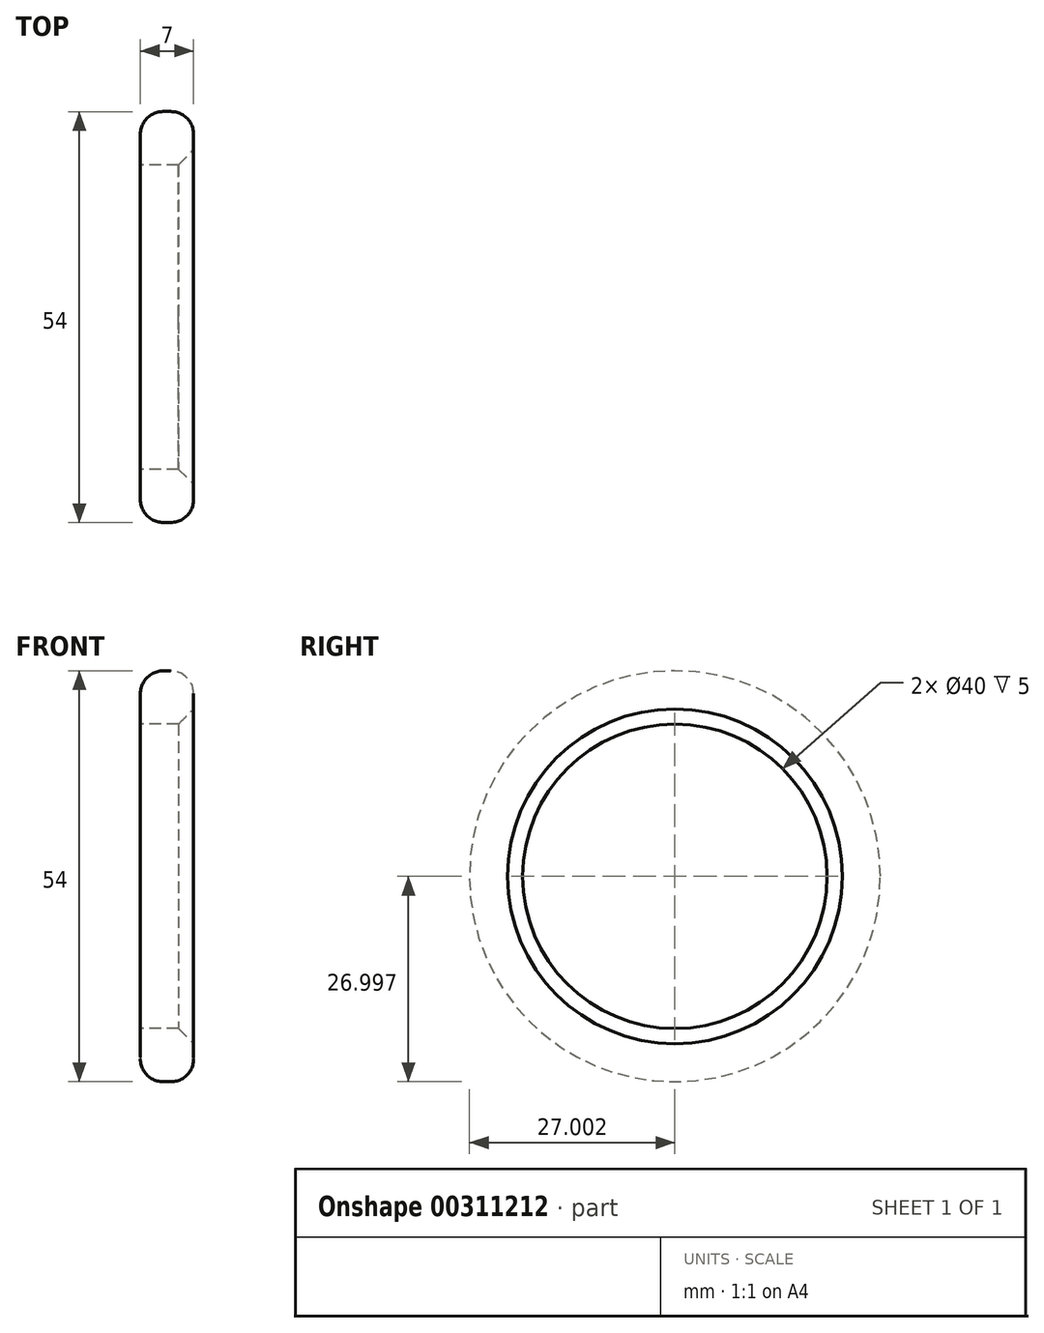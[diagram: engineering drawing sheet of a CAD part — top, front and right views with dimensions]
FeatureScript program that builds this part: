
annotation { "Feature Type Name" : "Feature", "Feature Type Description" : "" }
export const myFeature = defineFeature(function(context is Context, id is Id, definition is map)
    precondition{}
    {
        {
            var Q0;
            Q0=qCreatedBy(makeId("Top.planeOp"),FACE);
            var sketch = newSketch(context, id + "F0", { "sketchPlane" : qUnion([Q0])});
            skLineSegment(sketch, "E0", {"start": v(0, 0) * mm, "end": v(0, 4) * mm});
            skLineSegment(sketch, "E1", {"start": v(3, 7) * mm, "end": v(4, 7) * mm});
            skLineSegment(sketch, "E2", {"start": v(7, 4) * mm, "end": v(7, 2) * mm});
            skLineSegment(sketch, "E3", {"start": v(7, 2) * mm, "end": v(5, 0) * mm});
            skLineSegment(sketch, "E4", {"start": v(5, 0) * mm, "end": v(0, 0) * mm});
            skPoint(sketch, "E5.visualSharp", {"position": v(7, 7) * mm});
            skArc(sketch, "E5.filletArc", {"start": v(7, 4) * mm, "mid": v(6.12, 6.12) * mm, "end": v(4, 7) * mm});
            skPoint(sketch, "E6.visualSharp", {"position": v(0, 7) * mm});
            skArc(sketch, "E6.filletArc", {"start": v(3, 7) * mm, "mid": v(0.88, 6.12) * mm, "end": v(0, 4) * mm});
            skSolve(sketch);
        }
        {
            var Q0;
            Q0=qCreatedBy(makeId("Right.planeOp"),FACE);
            var sketch = newSketch(context, id + "F1", { "sketchPlane" : qUnion([Q0])});
            skCircle(sketch, "E7", {"center": v(-20, -0.3) * mm, "radius": 20 * mm});
            skPoint(sketch, "E7.first.point", {"position": v(0, 0) * mm});
            skPoint(sketch, "E7.second.point", {"position": v(-40, 0) * mm});
            skPoint(sketch, "E7.third.point", {"position": v(-20.22, 19.7) * mm});
            skSolve(sketch);
        }
        {
            var Q0;
            Q0=makeQuery(id+"F0.imprint","IMPRINT",FACE,{"disambiguationData":[TD([[makeQuery(id+"F0.imprint","IMPRINT",EDGE,{"derivedFrom":sQuery(id+"F0.wireOp",EDGE,"E0")}),-1.0]])]});
            var Q1;
            Q1=sQuery(id+"F1.wireOp",EDGE,"E7");
            revolve(context, id + "F2", {"entities" : qUnion([Q0]), "axis" : qUnion([Q1]), "revolveType" : RevolveType.FULL});
        }
        {
            var Q0;
            Q0=makeQuery(id+"F2.opRevolve","SWEPT_BODY",BODY,{"disambiguationData":[OSD([sQuery(id+"F0.wireOp",EDGE,"E0"),sQuery(id+"F0.wireOp",EDGE,"E1"),sQuery(id+"F0.wireOp",EDGE,"E2"),sQuery(id+"F0.wireOp",EDGE,"E3"),sQuery(id+"F0.wireOp",EDGE,"E4"),sQuery(id+"F0.wireOp",EDGE,"E5.filletArc"),sQuery(id+"F0.wireOp",EDGE,"E6.filletArc")])]});
            transform(context, id + "F3", {"entities" : qUnion([Q0]), "transformType" : TransformType.TRANSLATION_3D, "dx" : 0 * mm, "dy" : 0 * mm, "dz" : 0 * mm, "makeCopy" : true});
        }
    });
